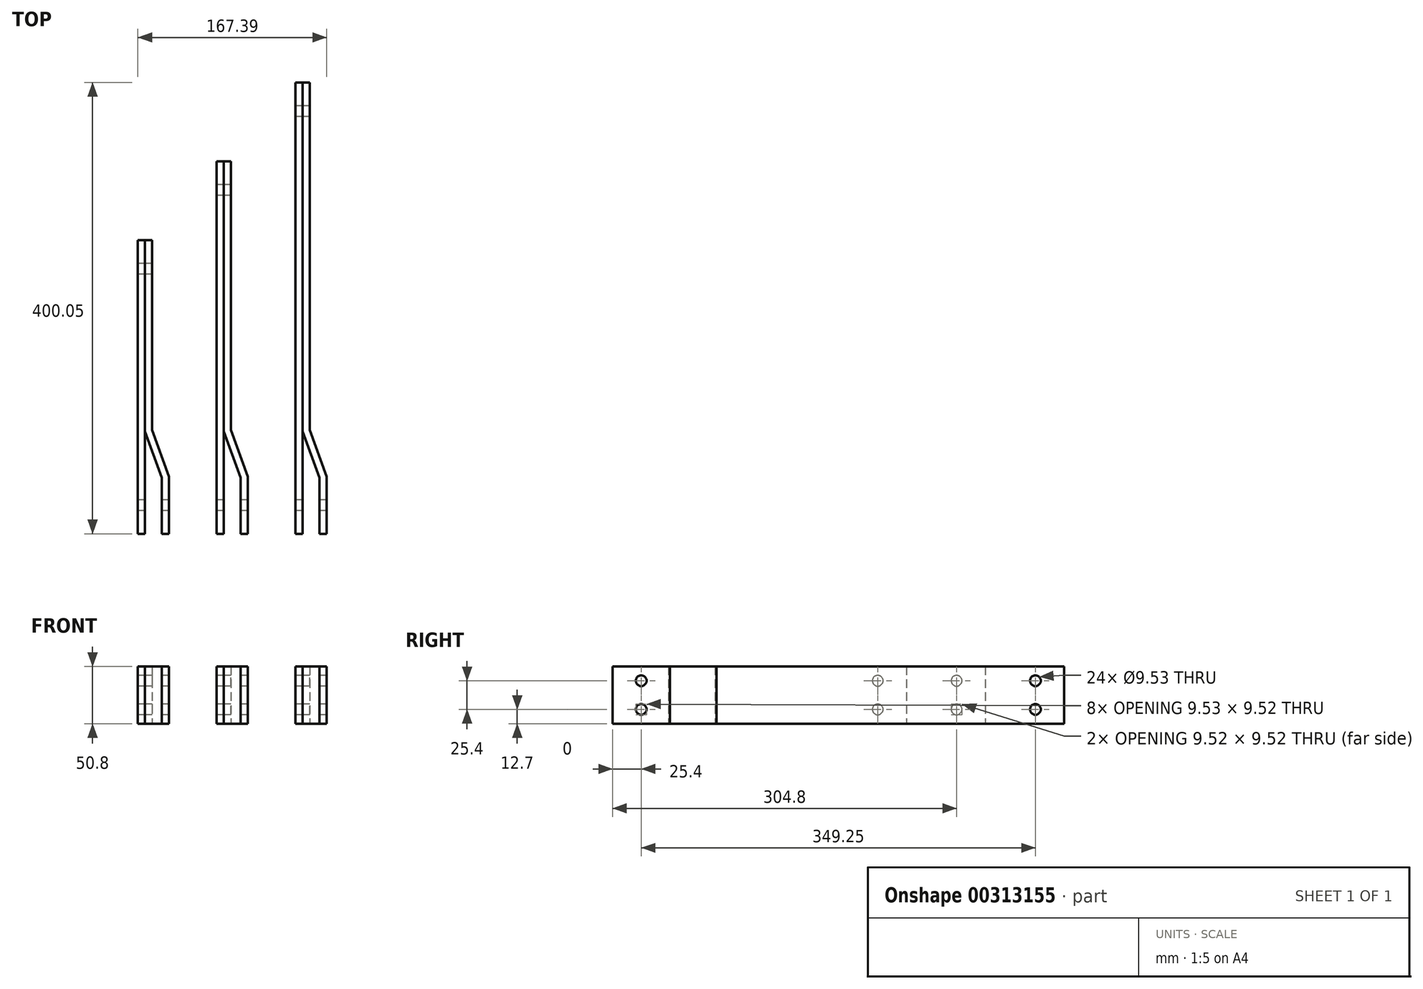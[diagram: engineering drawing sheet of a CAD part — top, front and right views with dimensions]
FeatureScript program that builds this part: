
annotation { "Feature Type Name" : "Feature", "Feature Type Description" : "" }
export const myFeature = defineFeature(function(context is Context, id is Id, definition is map)
    precondition{}
    {
        {
            var Q0;
            Q0=qCreatedBy(makeId("Top.planeOp"),FACE);
            var sketch = newSketch(context, id + "F0", { "sketchPlane" : qUnion([Q0])});
            skLineSegment(sketch, "E0.bottom", {"start": v(0, 260.35) * mm, "end": v(6.35, 260.35) * mm});
            skLineSegment(sketch, "E0.top", {"start": v(0, 0) * mm, "end": v(6.35, 0) * mm});
            skLineSegment(sketch, "E0.left", {"start": v(0, 260.35) * mm, "end": v(0, 0) * mm});
            skLineSegment(sketch, "E0.right", {"start": v(6.35, 260.35) * mm, "end": v(6.35, 0) * mm});
            skLineSegment(sketch, "E1.bottom", {"start": v(69.85, 330.2) * mm, "end": v(76.2, 330.2) * mm});
            skLineSegment(sketch, "E1.top", {"start": v(69.85, 0) * mm, "end": v(76.2, 0) * mm});
            skLineSegment(sketch, "E1.left", {"start": v(69.85, 330.2) * mm, "end": v(69.85, 0) * mm});
            skLineSegment(sketch, "E1.right", {"start": v(76.2, 330.2) * mm, "end": v(76.2, 0) * mm});
            skLineSegment(sketch, "E2.bottom", {"start": v(139.7, 400.05) * mm, "end": v(146.05, 400.05) * mm});
            skLineSegment(sketch, "E2.top", {"start": v(139.7, 0) * mm, "end": v(146.05, 0) * mm});
            skLineSegment(sketch, "E2.left", {"start": v(139.7, 400.05) * mm, "end": v(139.7, 0) * mm});
            skLineSegment(sketch, "E2.right", {"start": v(146.05, 400.05) * mm, "end": v(146.05, 0) * mm});
            skSolve(sketch);
        }
        {
            var Q0;
            Q0=qSketchRegion(id+"F0",true);
            extrude(context, id + "F1", {"entities" : qUnion([Q0]), "endBound" : BoundingType.SYMMETRIC, "depth" : 50.8 * mm});
        }
        {
            var Q0;
            Q0=qCreatedBy(makeId("Top.planeOp"),FACE);
            var sketch = newSketch(context, id + "F2", { "sketchPlane" : qUnion([Q0])});
            skLineSegment(sketch, "E3", {"start": v(21.34, 0) * mm, "end": v(27.69, 0) * mm});
            skLineSegment(sketch, "E4", {"start": v(27.69, 0) * mm, "end": v(27.69, 50.8) * mm});
            skLineSegment(sketch, "E5", {"start": v(27.69, 50.8) * mm, "end": v(12.7, 91.97) * mm});
            skLineSegment(sketch, "E6", {"start": v(12.7, 91.97) * mm, "end": v(12.7, 260.35) * mm});
            skLineSegment(sketch, "E7", {"start": v(12.7, 260.35) * mm, "end": v(6.35, 260.35) * mm});
            skLineSegment(sketch, "E8", {"start": v(6.35, 260.35) * mm, "end": v(6.35, 90.85) * mm});
            skLineSegment(sketch, "E9", {"start": v(6.35, 90.85) * mm, "end": v(21.34, 49.68) * mm});
            skLineSegment(sketch, "E10", {"start": v(21.34, 49.68) * mm, "end": v(21.34, 0) * mm});
            skLineSegment(sketch, "E11", {"start": v(91.19, 0) * mm, "end": v(97.54, 0) * mm});
            skLineSegment(sketch, "E12", {"start": v(97.54, 0) * mm, "end": v(97.54, 50.8) * mm});
            skLineSegment(sketch, "E13", {"start": v(97.54, 50.8) * mm, "end": v(82.55, 91.97) * mm});
            skLineSegment(sketch, "E14", {"start": v(76.2, 90.85) * mm, "end": v(91.19, 49.68) * mm});
            skLineSegment(sketch, "E15", {"start": v(91.19, 49.68) * mm, "end": v(91.19, 0) * mm});
            skLineSegment(sketch, "E16", {"start": v(161.04, 0) * mm, "end": v(167.39, 0) * mm});
            skLineSegment(sketch, "E17", {"start": v(167.39, 0) * mm, "end": v(167.39, 50.8) * mm});
            skLineSegment(sketch, "E18", {"start": v(167.39, 50.8) * mm, "end": v(152.4, 91.97) * mm});
            skLineSegment(sketch, "E19", {"start": v(146.05, 90.85) * mm, "end": v(161.04, 49.68) * mm});
            skLineSegment(sketch, "E20", {"start": v(161.04, 49.68) * mm, "end": v(161.04, 0) * mm});
            skLineSegment(sketch, "E21", {"start": v(76.2, 90.85) * mm, "end": v(76.2, 330.2) * mm});
            skLineSegment(sketch, "E22", {"start": v(76.2, 330.2) * mm, "end": v(82.55, 330.2) * mm});
            skLineSegment(sketch, "E23", {"start": v(82.55, 330.2) * mm, "end": v(82.55, 91.97) * mm});
            skLineSegment(sketch, "E24", {"start": v(146.05, 90.85) * mm, "end": v(146.05, 400.05) * mm});
            skLineSegment(sketch, "E25", {"start": v(146.05, 400.05) * mm, "end": v(152.4, 400.05) * mm});
            skLineSegment(sketch, "E26", {"start": v(152.4, 400.05) * mm, "end": v(152.4, 91.97) * mm});
            skSolve(sketch);
        }
        {
            var Q0;
            Q0 = qSketchRegion(id + "F2", true);
            extrude(context, id + "F3", {"entities" : qUnion([Q0]), "endBound" : BoundingType.SYMMETRIC, "depth" : 50.8 * mm});
        }
        {
            var Q0;
            Q0=makeQuery(id+"F1.opExtrude","SWEPT_FACE",FACE,{"disambiguationData":[OSD([sQuery(id+"F0.wireOp",EDGE,"E0.left")])]});
            var sketch = newSketch(context, id + "F4", { "sketchPlane" : qUnion([Q0])});
            skCircle(sketch, "E27", {"center": v(-25.4, 12.7) * mm, "radius": 4.76 * mm});
            skCircle(sketch, "E28", {"center": v(-25.4, -12.7) * mm, "radius": 4.76 * mm});
            skLineSegment(sketch, "E29", {"start": v(-25.4, 12.7) * mm, "end": v(-25.4, -12.7) * mm, "construction": true});
            skPoint(sketch, "E30", {"position": v(-25.4, 0) * mm});
            skSolve(sketch);
        }
        {
            var Q0;
            Q0 = qSketchRegion(id + "F4", true);
            extrude(context, id + "F5", {"entities" : qUnion([Q0]), "operationType" : NewBodyOperationType.REMOVE, "endBound" : BoundingType.THROUGH_ALL, "oppositeDirection" : true, "depth" : 25.4 * mm});
        }
        {
            var Q0;
            Q0=makeQuery(id+"F1.opExtrude","SWEPT_FACE",FACE,{"disambiguationData":[OSD([sQuery(id+"F0.wireOp",EDGE,"E0.left")])]});
            var sketch = newSketch(context, id + "F6", { "sketchPlane" : qUnion([Q0])});
            skCircle(sketch, "E31", {"center": v(-234.95, 12.7) * mm, "radius": 4.76 * mm});
            skCircle(sketch, "E32", {"center": v(-234.95, -12.7) * mm, "radius": 4.76 * mm});
            skLineSegment(sketch, "E33", {"start": v(-234.95, 12.7) * mm, "end": v(-234.95, -12.7) * mm, "construction": true});
            skPoint(sketch, "E34", {"position": v(-234.95, 0) * mm});
            skSolve(sketch);
        }
        {
            var Q0;
            Q0 = qSketchRegion(id + "F6", true);
            var Q1;
            Q1=makeQuery(id+"F3.opExtrude","SWEPT_FACE",FACE,{"disambiguationData":[OSD([sQuery(id+"F2.wireOp",EDGE,"E6")])]});
            extrude(context, id + "F7", {"entities" : qUnion([Q0]), "operationType" : NewBodyOperationType.REMOVE, "endBound" : BoundingType.UP_TO_SURFACE, "oppositeDirection" : true, "endBoundEntityFace" : qUnion([Q1]), "depth" : 25.4 * mm});
        }
        {
            var Q0;
            Q0=makeQuery(id+"F1.opExtrude","SWEPT_FACE",FACE,{"disambiguationData":[OSD([sQuery(id+"F0.wireOp",EDGE,"E1.left")])]});
            var sketch = newSketch(context, id + "F8", { "sketchPlane" : qUnion([Q0])});
            skCircle(sketch, "E35", {"center": v(-304.8, 12.7) * mm, "radius": 4.76 * mm});
            skCircle(sketch, "E36", {"center": v(-304.8, -12.7) * mm, "radius": 4.76 * mm});
            skLineSegment(sketch, "E37", {"start": v(-304.8, 12.7) * mm, "end": v(-304.8, -12.7) * mm, "construction": true});
            skPoint(sketch, "E38", {"position": v(-304.8, 0) * mm});
            skSolve(sketch);
        }
        {
            var Q0;
            Q0 = qSketchRegion(id + "F8", true);
            var Q1;
            Q1=makeQuery(id+"F3.opExtrude","SWEPT_FACE",FACE,{"disambiguationData":[OSD([sQuery(id+"F2.wireOp",EDGE,"E23")])]});
            extrude(context, id + "F9", {"entities" : qUnion([Q0]), "operationType" : NewBodyOperationType.REMOVE, "endBound" : BoundingType.UP_TO_SURFACE, "oppositeDirection" : true, "endBoundEntityFace" : qUnion([Q1]), "depth" : 25.4 * mm});
        }
        {
            var Q0;
            Q0=makeQuery(id+"F1.opExtrude","SWEPT_FACE",FACE,{"disambiguationData":[OSD([sQuery(id+"F0.wireOp",EDGE,"E2.left")])]});
            var sketch = newSketch(context, id + "F10", { "sketchPlane" : qUnion([Q0])});
            skCircle(sketch, "E39", {"center": v(-374.65, 12.7) * mm, "radius": 4.76 * mm});
            skCircle(sketch, "E40", {"center": v(-374.65, -12.7) * mm, "radius": 4.76 * mm});
            skLineSegment(sketch, "E41", {"start": v(-374.65, 12.7) * mm, "end": v(-374.65, -12.7) * mm, "construction": true});
            skPoint(sketch, "E42", {"position": v(-374.65, 0) * mm});
            skSolve(sketch);
        }
        {
            var Q0;
            Q0 = qSketchRegion(id + "F10", true);
            var Q1;
            Q1=makeQuery(id+"F3.opExtrude","SWEPT_FACE",FACE,{"disambiguationData":[OSD([sQuery(id+"F2.wireOp",EDGE,"E26")])]});
            extrude(context, id + "F11", {"entities" : qUnion([Q0]), "operationType" : NewBodyOperationType.REMOVE, "endBound" : BoundingType.UP_TO_SURFACE, "oppositeDirection" : true, "endBoundEntityFace" : qUnion([Q1]), "depth" : 25.4 * mm});
        }
    });
